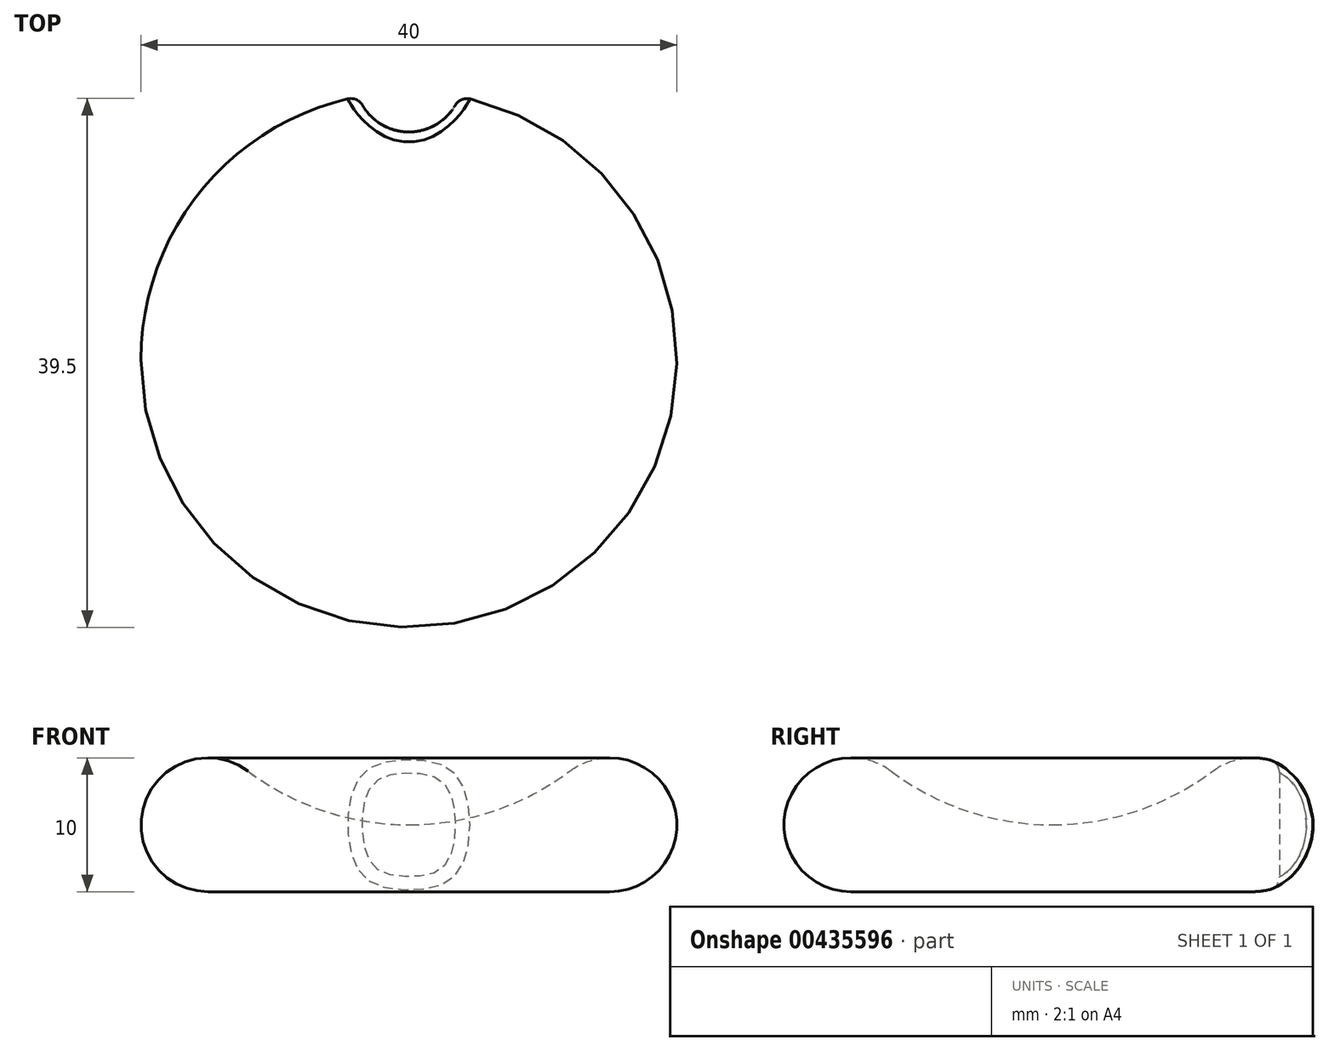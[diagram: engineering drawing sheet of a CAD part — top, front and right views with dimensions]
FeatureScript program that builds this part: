
annotation { "Feature Type Name" : "Feature", "Feature Type Description" : "" }
export const myFeature = defineFeature(function(context is Context, id is Id, definition is map)
    precondition{}
    {
        {
            var Q0;
            Q0=qCreatedBy(makeId("Front.planeOp"),FACE);
            var sketch = newSketch(context, id + "F0", { "sketchPlane" : qUnion([Q0])});
            skArc(sketch, "E0", {"start": v(-12, 9) * mm, "mid": v(-6.32, 6.03) * mm, "end": v(0, 5) * mm});
            skLineSegment(sketch, "E1", {"start": v(-15, 0) * mm, "end": v(0, 0) * mm});
            skLineSegment(sketch, "E2", {"start": v(0, 0) * mm, "end": v(0, 5) * mm});
            skArc(sketch, "E3", {"start": v(-12, 9) * mm, "mid": v(-19.74, 6.58) * mm, "end": v(-15, 0) * mm});
            skSolve(sketch);
        }
        {
            var Q0;
            Q0=makeQuery(id+"F0.imprint","IMPRINT",FACE,{"disambiguationData":[TD([[makeQuery(id+"F0.imprint","IMPRINT",EDGE,{"derivedFrom":sQuery(id+"F0.wireOp",EDGE,"E0")}),-1.0]])]});
            var Q1;
            Q1=sQuery(id+"F0.wireOp",EDGE,"E2");
            revolve(context, id + "F1", {"entities" : qUnion([Q0]), "axis" : qUnion([Q1]), "revolveType" : RevolveType.FULL});
        }
        {
            var Q0;
            Q0=qCreatedBy(makeId("Top.planeOp"),FACE);
            var sketch = newSketch(context, id + "F2", { "sketchPlane" : qUnion([Q0])});
            skCircle(sketch, "E4", {"center": v(0, 21) * mm, "radius": 4 * mm});
            skSolve(sketch);
        }
        {
            var Q0;
            Q0=makeQuery(id+"F2.imprint","IMPRINT",FACE,{"disambiguationData":[TD([[makeQuery(id+"F2.imprint","IMPRINT",EDGE,{"derivedFrom":sQuery(id+"F2.wireOp",EDGE,"E4")}),1.0]])]});
            extrude(context, id + "F3", {"entities" : qUnion([Q0]), "operationType" : NewBodyOperationType.REMOVE, "depth" : 25 * mm});
        }
        {
            var Q0;
            Q0=makeQuery(id+"F3.boolean.opBoolean","INTERSECT",EDGE,{"derivedFrom":[makeQuery(id+"F1.opRevolve","SWEPT_FACE",FACE,{"disambiguationData":[OSD([sQuery(id+"F0.wireOp",EDGE,"E3")])]}),makeQuery(id+"F3.opExtrude","SWEPT_FACE",FACE,{"disambiguationData":[OSD([sQuery(id+"F2.wireOp",EDGE,"E4")])]})]});
            fillet(context, id + "F4", {"entities" : qUnion([Q0]), "radius" : 1 * mm, "tangentPropagation" : true, "allowEdgeOverflow" : false});
        }
    });
